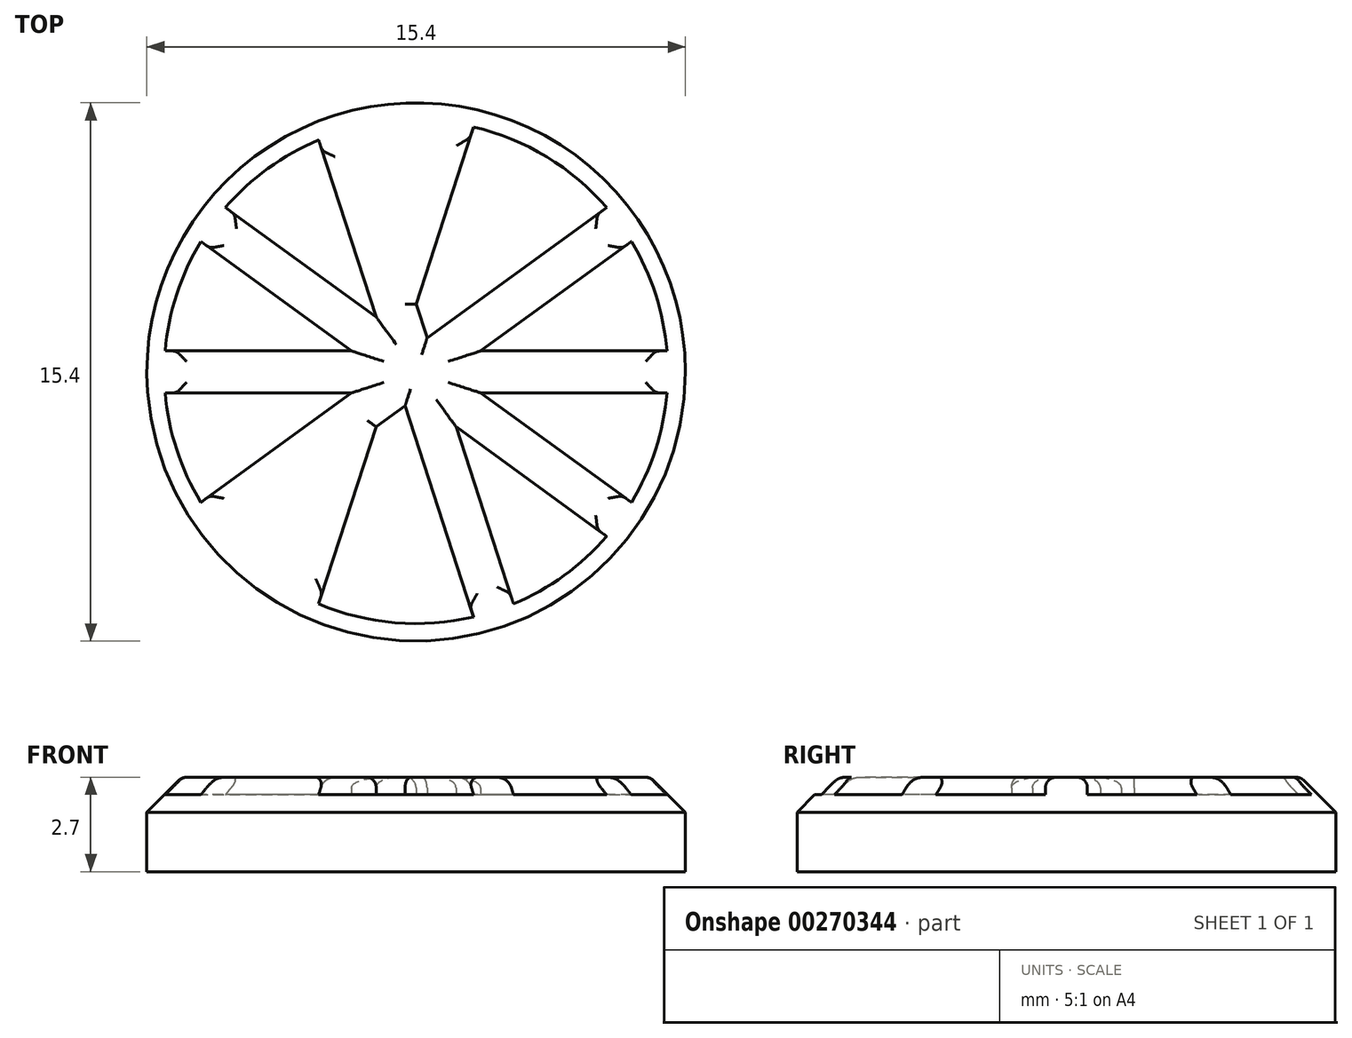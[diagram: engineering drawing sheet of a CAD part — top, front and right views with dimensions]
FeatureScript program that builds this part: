
annotation { "Feature Type Name" : "Feature", "Feature Type Description" : "" }
export const myFeature = defineFeature(function(context is Context, id is Id, definition is map)
    precondition{}
    {
        {
            var Q0;
            Q0=qCreatedBy(makeId("Top.planeOp"),FACE);
            var sketch = newSketch(context, id + "F0", { "sketchPlane" : qUnion([Q0])});
            skCircle(sketch, "E0", {"center": v(0, 0) * mm, "radius": 7.7 * mm});
            skSolve(sketch);
        }
        {
            var Q0;
            Q0 = qSketchRegion(id + "F0", true);
            extrude(context, id + "F1", {"entities" : qUnion([Q0]), "depth" : 2.2 * mm});
        }
        {
            var Q0;
            Q0=makeQuery(id+"F1.opExtrude","CAP_FACE",FACE,{"disambiguationData":[OSD([sQuery(id+"F0.wireOp",EDGE,"E0")])],"isStart":false});
            var sketch = newSketch(context, id + "F2", { "sketchPlane" : qUnion([Q0])});
            skLineSegment(sketch, "E1.bottom", {"start": v(-7.68, 0.6) * mm, "end": v(7.68, 0.6) * mm});
            skLineSegment(sketch, "E1.top", {"start": v(-7.68, -0.6) * mm, "end": v(7.68, -0.6) * mm});
            skLineSegment(sketch, "E1.left", {"start": v(-15, 0.6) * mm, "end": v(-15, -0.6) * mm});
            skLineSegment(sketch, "E1.right", {"start": v(15, 0.6) * mm, "end": v(15, -0.6) * mm});
            skPoint(sketch, "E1.middle", {"position": v(0, 0) * mm});
            skCircle(sketch, "E2.0.0", {"center": v(0, 0) * mm, "radius": 7.7 * mm});
            skLineSegment(sketch, "E3.1.0", {"start": v(-2.94, -7.12) * mm, "end": v(1.8, 7.49) * mm});
            skLineSegment(sketch, "E3.1.1", {"start": v(-1.8, -7.49) * mm, "end": v(2.94, 7.12) * mm});
            skLineSegment(sketch, "E3.2.0", {"start": v(5.86, -5) * mm, "end": v(-6.56, 4.03) * mm});
            skLineSegment(sketch, "E3.2.1", {"start": v(6.56, -4.03) * mm, "end": v(-5.86, 5) * mm});
            skLineSegment(sketch, "E3.3.0", {"start": v(6.56, 4.03) * mm, "end": v(-5.86, -5) * mm});
            skLineSegment(sketch, "E3.3.1", {"start": v(5.86, 5) * mm, "end": v(-6.56, -4.03) * mm});
            skLineSegment(sketch, "E3.4.0", {"start": v(-1.8, 7.49) * mm, "end": v(2.94, -7.12) * mm});
            skLineSegment(sketch, "E3.4.1", {"start": v(-2.94, 7.12) * mm, "end": v(1.8, -7.49) * mm});
            skPoint(sketch, "E4.orphan", {"position": v(-12.49, 8.33) * mm});
            skPoint(sketch, "E5.orphan", {"position": v(-11.78, 9.3) * mm});
            skPoint(sketch, "E6.orphan", {"position": v(-5.2, 14.08) * mm});
            skPoint(sketch, "E7.orphan", {"position": v(-4.06, 14.45) * mm});
            skPoint(sketch, "E8.orphan", {"position": v(4.06, 14.45) * mm});
            skPoint(sketch, "E9.orphan", {"position": v(5.2, 14.08) * mm});
            skPoint(sketch, "E10.orphan", {"position": v(-12.49, -8.33) * mm});
            skPoint(sketch, "E11.orphan", {"position": v(-11.78, -9.3) * mm});
            skPoint(sketch, "E12.orphan", {"position": v(-5.2, -14.08) * mm});
            skPoint(sketch, "E13.orphan", {"position": v(-4.06, -14.45) * mm});
            skPoint(sketch, "E14.orphan", {"position": v(4.06, -14.45) * mm});
            skPoint(sketch, "E15.orphan", {"position": v(5.2, -14.08) * mm});
            skPoint(sketch, "E16.orphan", {"position": v(11.78, -9.3) * mm});
            skPoint(sketch, "E17.orphan", {"position": v(12.49, -8.33) * mm});
            skPoint(sketch, "E18.orphan", {"position": v(12.49, 8.33) * mm});
            skPoint(sketch, "E19.orphan", {"position": v(11.78, 9.3) * mm});
            skSolve(sketch);
        }
        {
            var Q0;
            {var subQ1=sQuery(id+"F2.wireOp",EDGE,"E1.bottom");var subQ5=sQuery(id+"F2.wireOp",EDGE,"E2.0.0");var subQ6=makeQuery(id+"F2.imprint","INTERSECT",VERTEX,{"disambiguationData":[OD(0.0)],"derivedFrom":[subQ1,subQ5]});Q0=makeQuery(id+"F2.imprint","IMPRINT",FACE,{"disambiguationData":[TD([[makeQuery(id+"F2.imprint","IMPRINT",EDGE,{"disambiguationData":[TD([[subQ6,-1.0]])],"derivedFrom":subQ1}),-1.0]])]});}
            var Q1;
            {var subQ5=sQuery(id+"F2.wireOp",EDGE,"E3.2.0");var subQ7=sQuery(id+"F2.wireOp",EDGE,"E1.bottom");var subQ8=makeQuery(id+"F2.imprint","INTERSECT",VERTEX,{"derivedFrom":[subQ7,subQ5]});Q1=makeQuery(id+"F2.imprint","IMPRINT",FACE,{"disambiguationData":[TD([[makeQuery(id+"F2.imprint","IMPRINT",EDGE,{"disambiguationData":[TD([[subQ8,-1.0]])],"derivedFrom":subQ7}),1.0]])]});}
            var Q2;
            {var subQ0=sQuery(id+"F2.wireOp",EDGE,"E3.4.0");var subQ1=sQuery(id+"F2.wireOp",EDGE,"E2.0.0");var subQ2=makeQuery(id+"F2.imprint","INTERSECT",VERTEX,{"disambiguationData":[OD(0.0)],"derivedFrom":[subQ1,subQ0]});Q2=makeQuery(id+"F2.imprint","IMPRINT",FACE,{"disambiguationData":[TD([[makeQuery(id+"F2.imprint","IMPRINT",EDGE,{"disambiguationData":[TD([[subQ2,-1.0]])],"derivedFrom":subQ1}),1.0]])]});}
            var Q3;
            {var subQ5=sQuery(id+"F2.wireOp",EDGE,"E2.0.0");var subQ7=sQuery(id+"F2.wireOp",EDGE,"E3.1.0");var subQ8=makeQuery(id+"F2.imprint","INTERSECT",VERTEX,{"disambiguationData":[OD(1.0)],"derivedFrom":[subQ5,subQ7]});Q3=makeQuery(id+"F2.imprint","IMPRINT",FACE,{"disambiguationData":[TD([[makeQuery(id+"F2.imprint","IMPRINT",EDGE,{"disambiguationData":[TD([[subQ8,1.0]])],"derivedFrom":subQ5}),1.0]])]});}
            var Q4;
            {var subQ3=sQuery(id+"F2.wireOp",EDGE,"E1.bottom");var subQ7=sQuery(id+"F2.wireOp",EDGE,"E3.1.1");var subQ8=makeQuery(id+"F2.imprint","INTERSECT",VERTEX,{"derivedFrom":[subQ3,subQ7]});Q4=makeQuery(id+"F2.imprint","IMPRINT",FACE,{"disambiguationData":[TD([[makeQuery(id+"F2.imprint","IMPRINT",EDGE,{"disambiguationData":[TD([[subQ8,-1.0]])],"derivedFrom":subQ3}),1.0]])]});}
            var Q5;
            {var subQ5=sQuery(id+"F2.wireOp",EDGE,"E2.0.0");var subQ6=sQuery(id+"F2.wireOp",EDGE,"E1.bottom");var subQ7=makeQuery(id+"F2.imprint","INTERSECT",VERTEX,{"disambiguationData":[OD(1.0)],"derivedFrom":[subQ6,subQ5]});Q5=makeQuery(id+"F2.imprint","IMPRINT",FACE,{"disambiguationData":[TD([[makeQuery(id+"F2.imprint","IMPRINT",EDGE,{"disambiguationData":[TD([[subQ7,1.0]])],"derivedFrom":subQ6}),-1.0]])]});}
            var Q6;
            {var subQ3=sQuery(id+"F2.wireOp",EDGE,"E1.top");var subQ7=sQuery(id+"F2.wireOp",EDGE,"E3.4.0");var subQ9=makeQuery(id+"F2.imprint","INTERSECT",VERTEX,{"derivedFrom":[subQ3,subQ7]});Q6=makeQuery(id+"F2.imprint","IMPRINT",FACE,{"disambiguationData":[TD([[makeQuery(id+"F2.imprint","IMPRINT",EDGE,{"disambiguationData":[TD([[subQ9,-1.0]])],"derivedFrom":subQ3}),-1.0]])]});}
            var Q7;
            {var subQ0=sQuery(id+"F2.wireOp",EDGE,"E3.4.0");var subQ1=sQuery(id+"F2.wireOp",EDGE,"E2.0.0");var subQ2=makeQuery(id+"F2.imprint","INTERSECT",VERTEX,{"disambiguationData":[OD(1.0)],"derivedFrom":[subQ1,subQ0]});Q7=makeQuery(id+"F2.imprint","IMPRINT",FACE,{"disambiguationData":[TD([[makeQuery(id+"F2.imprint","IMPRINT",EDGE,{"disambiguationData":[TD([[subQ2,1.0]])],"derivedFrom":subQ1}),1.0]])]});}
            var Q8;
            {var subQ1=sQuery(id+"F2.wireOp",EDGE,"E2.0.0");var subQ5=sQuery(id+"F2.wireOp",EDGE,"E3.1.0");var subQ6=makeQuery(id+"F2.imprint","INTERSECT",VERTEX,{"disambiguationData":[OD(0.0)],"derivedFrom":[subQ1,subQ5]});Q8=makeQuery(id+"F2.imprint","IMPRINT",FACE,{"disambiguationData":[TD([[makeQuery(id+"F2.imprint","IMPRINT",EDGE,{"disambiguationData":[TD([[subQ6,-1.0]])],"derivedFrom":subQ1}),1.0]])]});}
            var Q9;
            {var subQ5=sQuery(id+"F2.wireOp",EDGE,"E1.top");var subQ7=sQuery(id+"F2.wireOp",EDGE,"E3.3.1");var subQ9=makeQuery(id+"F2.imprint","INTERSECT",VERTEX,{"derivedFrom":[subQ5,subQ7]});Q9=makeQuery(id+"F2.imprint","IMPRINT",FACE,{"disambiguationData":[TD([[makeQuery(id+"F2.imprint","IMPRINT",EDGE,{"disambiguationData":[TD([[subQ9,-1.0]])],"derivedFrom":subQ5}),-1.0]])]});}
            var Q10;
            {var subQ0=sQuery(id+"F2.wireOp",EDGE,"E3.3.1");var subQ1=sQuery(id+"F2.wireOp",EDGE,"E1.top");var subQ2=makeQuery(id+"F2.imprint","INTERSECT",VERTEX,{"derivedFrom":[subQ1,subQ0]});Q10=makeQuery(id+"F2.imprint","IMPRINT",FACE,{"disambiguationData":[TD([[makeQuery(id+"F2.imprint","IMPRINT",EDGE,{"disambiguationData":[TD([[subQ2,-1.0]])],"derivedFrom":subQ1}),1.0]])]});}
            var Q11;
            {var subQ0=sQuery(id+"F2.wireOp",EDGE,"E3.2.0");var subQ1=sQuery(id+"F2.wireOp",EDGE,"E1.bottom");var subQ2=makeQuery(id+"F2.imprint","INTERSECT",VERTEX,{"derivedFrom":[subQ1,subQ0]});Q11=makeQuery(id+"F2.imprint","IMPRINT",FACE,{"disambiguationData":[TD([[makeQuery(id+"F2.imprint","IMPRINT",EDGE,{"disambiguationData":[TD([[subQ2,-1.0]])],"derivedFrom":subQ1}),-1.0]])]});}
            var Q12;
            {var subQ0=sQuery(id+"F2.wireOp",EDGE,"E3.4.1");var subQ1=sQuery(id+"F2.wireOp",EDGE,"E1.bottom");var subQ2=makeQuery(id+"F2.imprint","INTERSECT",VERTEX,{"derivedFrom":[subQ1,subQ0]});Q12=makeQuery(id+"F2.imprint","IMPRINT",FACE,{"disambiguationData":[TD([[makeQuery(id+"F2.imprint","IMPRINT",EDGE,{"disambiguationData":[TD([[subQ2,-1.0]])],"derivedFrom":subQ1}),1.0]])]});}
            var Q13;
            {var subQ0=sQuery(id+"F2.wireOp",EDGE,"E3.2.1");var subQ1=sQuery(id+"F2.wireOp",EDGE,"E3.1.0");var subQ2=makeQuery(id+"F2.imprint","INTERSECT",VERTEX,{"derivedFrom":[subQ1,subQ0]});Q13=makeQuery(id+"F2.imprint","IMPRINT",FACE,{"disambiguationData":[TD([[makeQuery(id+"F2.imprint","IMPRINT",EDGE,{"disambiguationData":[TD([[subQ2,-1.0]])],"derivedFrom":subQ1}),-1.0]])]});}
            var Q14;
            {var subQ0=sQuery(id+"F2.wireOp",EDGE,"E3.4.0");var subQ1=sQuery(id+"F2.wireOp",EDGE,"E1.bottom");var subQ2=makeQuery(id+"F2.imprint","INTERSECT",VERTEX,{"derivedFrom":[subQ1,subQ0]});Q14=makeQuery(id+"F2.imprint","IMPRINT",FACE,{"disambiguationData":[TD([[makeQuery(id+"F2.imprint","IMPRINT",EDGE,{"disambiguationData":[TD([[subQ2,-1.0]])],"derivedFrom":subQ1}),1.0]])]});}
            var Q15;
            {var subQ0=sQuery(id+"F2.wireOp",EDGE,"E3.1.1");var subQ1=sQuery(id+"F2.wireOp",EDGE,"E1.bottom");var subQ2=makeQuery(id+"F2.imprint","INTERSECT",VERTEX,{"derivedFrom":[subQ1,subQ0]});Q15=makeQuery(id+"F2.imprint","IMPRINT",FACE,{"disambiguationData":[TD([[makeQuery(id+"F2.imprint","IMPRINT",EDGE,{"disambiguationData":[TD([[subQ2,-1.0]])],"derivedFrom":subQ1}),-1.0]])]});}
            var Q16;
            {var subQ0=sQuery(id+"F2.wireOp",EDGE,"E3.4.0");var subQ1=sQuery(id+"F2.wireOp",EDGE,"E1.top");var subQ2=makeQuery(id+"F2.imprint","INTERSECT",VERTEX,{"derivedFrom":[subQ1,subQ0]});Q16=makeQuery(id+"F2.imprint","IMPRINT",FACE,{"disambiguationData":[TD([[makeQuery(id+"F2.imprint","IMPRINT",EDGE,{"disambiguationData":[TD([[subQ2,-1.0]])],"derivedFrom":subQ1}),1.0]])]});}
            var Q17;
            {var subQ0=sQuery(id+"F2.wireOp",EDGE,"E3.1.1");var subQ1=sQuery(id+"F2.wireOp",EDGE,"E1.top");var subQ2=makeQuery(id+"F2.imprint","INTERSECT",VERTEX,{"derivedFrom":[subQ1,subQ0]});Q17=makeQuery(id+"F2.imprint","IMPRINT",FACE,{"disambiguationData":[TD([[makeQuery(id+"F2.imprint","IMPRINT",EDGE,{"disambiguationData":[TD([[subQ2,-1.0]])],"derivedFrom":subQ1}),-1.0]])]});}
            var Q18;
            {var subQ0=sQuery(id+"F2.wireOp",EDGE,"E3.4.1");var subQ1=sQuery(id+"F2.wireOp",EDGE,"E3.1.1");var subQ2=makeQuery(id+"F2.imprint","INTERSECT",VERTEX,{"derivedFrom":[subQ1,subQ0]});Q18=makeQuery(id+"F2.imprint","IMPRINT",FACE,{"disambiguationData":[TD([[makeQuery(id+"F2.imprint","IMPRINT",EDGE,{"disambiguationData":[TD([[subQ2,-1.0]])],"derivedFrom":subQ1}),1.0]])]});}
            var Q19;
            {var subQ0=sQuery(id+"F2.wireOp",EDGE,"E3.1.0");var subQ1=sQuery(id+"F2.wireOp",EDGE,"E1.top");var subQ2=makeQuery(id+"F2.imprint","INTERSECT",VERTEX,{"derivedFrom":[subQ1,subQ0]});Q19=makeQuery(id+"F2.imprint","IMPRINT",FACE,{"disambiguationData":[TD([[makeQuery(id+"F2.imprint","IMPRINT",EDGE,{"disambiguationData":[TD([[subQ2,-1.0]])],"derivedFrom":subQ1}),-1.0]])]});}
            var Q20;
            {var subQ0=sQuery(id+"F2.wireOp",EDGE,"E3.1.0");var subQ1=sQuery(id+"F2.wireOp",EDGE,"E1.top");var subQ2=makeQuery(id+"F2.imprint","INTERSECT",VERTEX,{"derivedFrom":[subQ1,subQ0]});Q20=makeQuery(id+"F2.imprint","IMPRINT",FACE,{"disambiguationData":[TD([[makeQuery(id+"F2.imprint","IMPRINT",EDGE,{"disambiguationData":[TD([[subQ2,-1.0]])],"derivedFrom":subQ1}),1.0]])]});}
            var Q21;
            {var subQ0=sQuery(id+"F2.wireOp",EDGE,"E3.4.1");var subQ1=sQuery(id+"F2.wireOp",EDGE,"E1.top");var subQ2=makeQuery(id+"F2.imprint","INTERSECT",VERTEX,{"derivedFrom":[subQ1,subQ0]});Q21=makeQuery(id+"F2.imprint","IMPRINT",FACE,{"disambiguationData":[TD([[makeQuery(id+"F2.imprint","IMPRINT",EDGE,{"disambiguationData":[TD([[subQ2,-1.0]])],"derivedFrom":subQ1}),-1.0]])]});}
            var Q22;
            {var subQ0=sQuery(id+"F2.wireOp",EDGE,"E3.3.0");var subQ1=sQuery(id+"F2.wireOp",EDGE,"E1.top");var subQ2=makeQuery(id+"F2.imprint","INTERSECT",VERTEX,{"derivedFrom":[subQ1,subQ0]});Q22=makeQuery(id+"F2.imprint","IMPRINT",FACE,{"disambiguationData":[TD([[makeQuery(id+"F2.imprint","IMPRINT",EDGE,{"disambiguationData":[TD([[subQ2,-1.0]])],"derivedFrom":subQ1}),-1.0]])]});}
            var Q23;
            {var subQ0=sQuery(id+"F2.wireOp",EDGE,"E3.1.1");var subQ1=sQuery(id+"F2.wireOp",EDGE,"E1.top");var subQ2=makeQuery(id+"F2.imprint","INTERSECT",VERTEX,{"derivedFrom":[subQ1,subQ0]});Q23=makeQuery(id+"F2.imprint","IMPRINT",FACE,{"disambiguationData":[TD([[makeQuery(id+"F2.imprint","IMPRINT",EDGE,{"disambiguationData":[TD([[subQ2,-1.0]])],"derivedFrom":subQ1}),1.0]])]});}
            var Q24;
            {var subQ0=sQuery(id+"F2.wireOp",EDGE,"E3.4.0");var subQ1=sQuery(id+"F2.wireOp",EDGE,"E3.1.1");var subQ2=makeQuery(id+"F2.imprint","INTERSECT",VERTEX,{"derivedFrom":[subQ1,subQ0]});Q24=makeQuery(id+"F2.imprint","IMPRINT",FACE,{"disambiguationData":[TD([[makeQuery(id+"F2.imprint","IMPRINT",EDGE,{"disambiguationData":[TD([[subQ2,-1.0]])],"derivedFrom":subQ1}),-1.0]])]});}
            var Q25;
            {var subQ0=sQuery(id+"F2.wireOp",EDGE,"E3.4.0");var subQ1=sQuery(id+"F2.wireOp",EDGE,"E1.bottom");var subQ2=makeQuery(id+"F2.imprint","INTERSECT",VERTEX,{"derivedFrom":[subQ1,subQ0]});Q25=makeQuery(id+"F2.imprint","IMPRINT",FACE,{"disambiguationData":[TD([[makeQuery(id+"F2.imprint","IMPRINT",EDGE,{"disambiguationData":[TD([[subQ2,-1.0]])],"derivedFrom":subQ1}),-1.0]])]});}
            var Q26;
            {var subQ0=sQuery(id+"F2.wireOp",EDGE,"E3.2.1");var subQ1=sQuery(id+"F2.wireOp",EDGE,"E1.bottom");var subQ2=makeQuery(id+"F2.imprint","INTERSECT",VERTEX,{"derivedFrom":[subQ1,subQ0]});Q26=makeQuery(id+"F2.imprint","IMPRINT",FACE,{"disambiguationData":[TD([[makeQuery(id+"F2.imprint","IMPRINT",EDGE,{"disambiguationData":[TD([[subQ2,-1.0]])],"derivedFrom":subQ1}),1.0]])]});}
            var Q27;
            {var subQ0=sQuery(id+"F2.wireOp",EDGE,"E3.1.0");var subQ1=sQuery(id+"F2.wireOp",EDGE,"E1.bottom");var subQ2=makeQuery(id+"F2.imprint","INTERSECT",VERTEX,{"derivedFrom":[subQ1,subQ0]});Q27=makeQuery(id+"F2.imprint","IMPRINT",FACE,{"disambiguationData":[TD([[makeQuery(id+"F2.imprint","IMPRINT",EDGE,{"disambiguationData":[TD([[subQ2,-1.0]])],"derivedFrom":subQ1}),1.0]])]});}
            var Q28;
            {var subQ0=sQuery(id+"F2.wireOp",EDGE,"E3.4.1");var subQ1=sQuery(id+"F2.wireOp",EDGE,"E1.bottom");var subQ2=makeQuery(id+"F2.imprint","INTERSECT",VERTEX,{"derivedFrom":[subQ1,subQ0]});Q28=makeQuery(id+"F2.imprint","IMPRINT",FACE,{"disambiguationData":[TD([[makeQuery(id+"F2.imprint","IMPRINT",EDGE,{"disambiguationData":[TD([[subQ2,-1.0]])],"derivedFrom":subQ1}),-1.0]])]});}
            var Q29;
            {var subQ0=sQuery(id+"F2.wireOp",EDGE,"E3.2.0");var subQ1=sQuery(id+"F2.wireOp",EDGE,"E3.1.0");var subQ2=makeQuery(id+"F2.imprint","INTERSECT",VERTEX,{"derivedFrom":[subQ1,subQ0]});Q29=makeQuery(id+"F2.imprint","IMPRINT",FACE,{"disambiguationData":[TD([[makeQuery(id+"F2.imprint","IMPRINT",EDGE,{"disambiguationData":[TD([[subQ2,-1.0]])],"derivedFrom":subQ1}),1.0]])]});}
            var Q30;
            {var subQ0=sQuery(id+"F2.wireOp",EDGE,"E3.2.0");var subQ1=sQuery(id+"F2.wireOp",EDGE,"E3.1.0");var subQ2=makeQuery(id+"F2.imprint","INTERSECT",VERTEX,{"derivedFrom":[subQ1,subQ0]});Q30=makeQuery(id+"F2.imprint","IMPRINT",FACE,{"disambiguationData":[TD([[makeQuery(id+"F2.imprint","IMPRINT",EDGE,{"disambiguationData":[TD([[subQ2,-1.0]])],"derivedFrom":subQ1}),-1.0]])]});}
            var Q31;
            {var subQ0=sQuery(id+"F2.wireOp",EDGE,"E3.4.1");var subQ1=sQuery(id+"F2.wireOp",EDGE,"E1.top");var subQ2=makeQuery(id+"F2.imprint","INTERSECT",VERTEX,{"derivedFrom":[subQ1,subQ0]});Q31=makeQuery(id+"F2.imprint","IMPRINT",FACE,{"disambiguationData":[TD([[makeQuery(id+"F2.imprint","IMPRINT",EDGE,{"disambiguationData":[TD([[subQ2,-1.0]])],"derivedFrom":subQ1}),1.0]])]});}
            var Q32;
            {var subQ0=sQuery(id+"F2.wireOp",EDGE,"E3.2.0");var subQ1=sQuery(id+"F2.wireOp",EDGE,"E1.top");var subQ2=makeQuery(id+"F2.imprint","INTERSECT",VERTEX,{"derivedFrom":[subQ1,subQ0]});Q32=makeQuery(id+"F2.imprint","IMPRINT",FACE,{"disambiguationData":[TD([[makeQuery(id+"F2.imprint","IMPRINT",EDGE,{"disambiguationData":[TD([[subQ2,-1.0]])],"derivedFrom":subQ1}),-1.0]])]});}
            var Q33;
            {var subQ0=sQuery(id+"F2.wireOp",EDGE,"E3.3.0");var subQ1=sQuery(id+"F2.wireOp",EDGE,"E1.top");var subQ2=makeQuery(id+"F2.imprint","INTERSECT",VERTEX,{"derivedFrom":[subQ1,subQ0]});Q33=makeQuery(id+"F2.imprint","IMPRINT",FACE,{"disambiguationData":[TD([[makeQuery(id+"F2.imprint","IMPRINT",EDGE,{"disambiguationData":[TD([[subQ2,-1.0]])],"derivedFrom":subQ1}),1.0]])]});}
            var Q34;
            {var subQ0=sQuery(id+"F2.wireOp",EDGE,"E3.3.0");var subQ1=sQuery(id+"F2.wireOp",EDGE,"E3.1.1");var subQ2=makeQuery(id+"F2.imprint","INTERSECT",VERTEX,{"derivedFrom":[subQ1,subQ0]});Q34=makeQuery(id+"F2.imprint","IMPRINT",FACE,{"disambiguationData":[TD([[makeQuery(id+"F2.imprint","IMPRINT",EDGE,{"disambiguationData":[TD([[subQ2,-1.0]])],"derivedFrom":subQ1}),-1.0]])]});}
            var Q35;
            {var subQ0=sQuery(id+"F2.wireOp",EDGE,"E3.4.0");var subQ1=sQuery(id+"F2.wireOp",EDGE,"E3.1.1");var subQ2=makeQuery(id+"F2.imprint","INTERSECT",VERTEX,{"derivedFrom":[subQ1,subQ0]});Q35=makeQuery(id+"F2.imprint","IMPRINT",FACE,{"disambiguationData":[TD([[makeQuery(id+"F2.imprint","IMPRINT",EDGE,{"disambiguationData":[TD([[subQ2,-1.0]])],"derivedFrom":subQ1}),1.0]])]});}
            var Q36;
            {var subQ0=sQuery(id+"F2.wireOp",EDGE,"E3.2.1");var subQ1=sQuery(id+"F2.wireOp",EDGE,"E1.bottom");var subQ2=makeQuery(id+"F2.imprint","INTERSECT",VERTEX,{"derivedFrom":[subQ1,subQ0]});Q36=makeQuery(id+"F2.imprint","IMPRINT",FACE,{"disambiguationData":[TD([[makeQuery(id+"F2.imprint","IMPRINT",EDGE,{"disambiguationData":[TD([[subQ2,-1.0]])],"derivedFrom":subQ1}),-1.0]])]});}
            var Q37;
            {var subQ0=sQuery(id+"F2.wireOp",EDGE,"E3.3.1");var subQ1=sQuery(id+"F2.wireOp",EDGE,"E1.bottom");var subQ2=makeQuery(id+"F2.imprint","INTERSECT",VERTEX,{"derivedFrom":[subQ1,subQ0]});Q37=makeQuery(id+"F2.imprint","IMPRINT",FACE,{"disambiguationData":[TD([[makeQuery(id+"F2.imprint","IMPRINT",EDGE,{"disambiguationData":[TD([[subQ2,-1.0]])],"derivedFrom":subQ1}),1.0]])]});}
            var Q38;
            {var subQ0=sQuery(id+"F2.wireOp",EDGE,"E3.1.0");var subQ1=sQuery(id+"F2.wireOp",EDGE,"E1.bottom");var subQ2=makeQuery(id+"F2.imprint","INTERSECT",VERTEX,{"derivedFrom":[subQ1,subQ0]});Q38=makeQuery(id+"F2.imprint","IMPRINT",FACE,{"disambiguationData":[TD([[makeQuery(id+"F2.imprint","IMPRINT",EDGE,{"disambiguationData":[TD([[subQ2,-1.0]])],"derivedFrom":subQ1}),-1.0]])]});}
            var Q39;
            {var subQ0=sQuery(id+"F2.wireOp",EDGE,"E3.4.1");var subQ1=sQuery(id+"F2.wireOp",EDGE,"E3.1.0");var subQ2=makeQuery(id+"F2.imprint","INTERSECT",VERTEX,{"derivedFrom":[subQ1,subQ0]});Q39=makeQuery(id+"F2.imprint","IMPRINT",FACE,{"disambiguationData":[TD([[makeQuery(id+"F2.imprint","IMPRINT",EDGE,{"disambiguationData":[TD([[subQ2,-1.0]])],"derivedFrom":subQ1}),1.0]])]});}
            var Q40;
            {var subQ8=sQuery(id+"F2.wireOp",EDGE,"E3.3.1");var subQ14=sQuery(id+"F2.wireOp",EDGE,"E1.bottom");var subQ15=makeQuery(id+"F2.imprint","INTERSECT",VERTEX,{"derivedFrom":[subQ14,subQ8]});Q40=makeQuery(id+"F2.imprint","IMPRINT",FACE,{"disambiguationData":[TD([[makeQuery(id+"F2.imprint","IMPRINT",EDGE,{"disambiguationData":[TD([[subQ15,-1.0]])],"derivedFrom":subQ14}),-1.0]])]});}
            extrude(context, id + "F3", {"entities" : qUnion([Q0, Q1, Q2, Q3, Q4, Q5, Q6, Q7, Q8, Q9, Q10, Q11, Q12, Q13, Q14, Q15, Q16, Q17, Q18, Q19, Q20, Q21, Q22, Q23, Q24, Q25, Q26, Q27, Q28, Q29, Q30, Q31, Q32, Q33, Q34, Q35, Q36, Q37, Q38, Q39, Q40]), "operationType" : NewBodyOperationType.ADD, "depth" : 0.5 * mm});
        }
        {
            var Q0;
            {var subQ0=sQuery(id+"F2.wireOp",EDGE,"E2.0.0");Q0=makeQuery(id+"F3.opExtrude","CAP_EDGE",EDGE,{"disambiguationData":[OSD([subQ0]),TDD([makeQuery(id+"F2.imprint","IMPRINT",EDGE,{"disambiguationData":[TD([[makeQuery(id+"F2.imprint","INTERSECT",VERTEX,{"disambiguationData":[OD(0.0)],"derivedFrom":[sQuery(id+"F2.wireOp",EDGE,"E1.bottom"),subQ0]}),-1.0]])],"derivedFrom":subQ0})])],"isStart":false});}
            chamfer(context, id + "F4", {"entities" : qUnion([Q0]), "width" : 1 * mm, "tangentPropagation" : true});
        }
        {
            var Q0;
            Q0=makeQuery(id+"F3.opExtrude","CAP_FACE",FACE,{"disambiguationData":[OSD([sQuery(id+"F2.wireOp",EDGE,"E1.bottom"),sQuery(id+"F2.wireOp",EDGE,"E1.top"),sQuery(id+"F2.wireOp",EDGE,"E2.0.0"),sQuery(id+"F2.wireOp",EDGE,"E3.1.0"),sQuery(id+"F2.wireOp",EDGE,"E3.1.1"),sQuery(id+"F2.wireOp",EDGE,"E3.2.0"),sQuery(id+"F2.wireOp",EDGE,"E3.2.1"),sQuery(id+"F2.wireOp",EDGE,"E3.3.0"),sQuery(id+"F2.wireOp",EDGE,"E3.3.1"),sQuery(id+"F2.wireOp",EDGE,"E3.4.0"),sQuery(id+"F2.wireOp",EDGE,"E3.4.1")])],"isStart":false});
            fillet(context, id + "F5", {"entities" : qUnion([Q0]), "radius" : 0.3 * mm, "tangentPropagation" : true, "allowEdgeOverflow" : false});
        }
    });
